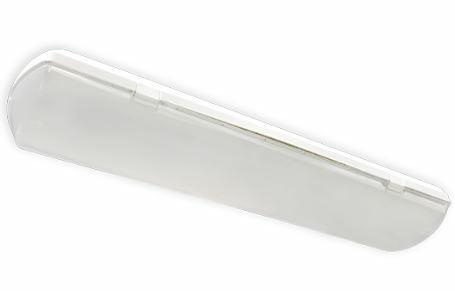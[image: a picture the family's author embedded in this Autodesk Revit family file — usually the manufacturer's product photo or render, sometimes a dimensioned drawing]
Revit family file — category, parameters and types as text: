
# Revit family: SCALED
name_source: partatom
category: Lighting Fixtures
revit_build: Autodesk Revit LT 2017 (Build: 20160225_1515(x64)
units: mm (PartAtom-declared; Revit-internal decimal feet)

## family parameters
Cut with Voids When Loaded = No
Host = Face
Light Source = Yes
Part Type = Normal
Room Calculation Point = No
Round Connector Dimension = Use Diameter
Shared = No

## types (4) — shared parameters
Color Filter = 16777215
Default Elevation = 4' - 0"
Dimming Lamp Color Temperature Shift = <None>
Emit from Line Length = 2' - 0"
Lamp = LED
Manufacturer = BEGHELLI
Model = BS100LED2
Tilt Angle = -90.00°
Type Image = BS100LED2 PICTURE.JPG

## per-type parameters (varying)
| type | Photometric Web File | Wattage Comments |
| SCALED2HTLOWT40120-270V | BS100LED2HTLOWT40120-277V_S.ies | 30W |
| SCALED2HTHOWT40120-270V | BS100LED2HTHOWT40120-277V_S.ies | 50W |
| SCALED2HTMOWT40120-270V | BS100LED2HTMOWT40120-277V_S.ies | 40W |
| SCALED2SAWT40120-270V | BS100LED2SAWT40120-277V_S.ies | 10W |

## geometry (parser evidence)
native form markers: Sweep x33
no freeform markers — native parametric forms only
